# Revit family: AFX-Metropolitan-Semi_Flush
name_source: partatom
category: Lighting Fixtures
units: mm (PartAtom-declared; Revit-internal decimal feet)

## family parameters
Cut with Voids When Loaded = No
Host = Face
Light Source = No
Maintain Annotation Orientation = No
Part Type = Normal
Room Calculation Point = No
Round Connector Dimension = Use Diameter
Shared = No

## types (1)
- METC15
    Apparent Load = 0 VA
    Assembly Code = D5020200
    Canopy Finish = AFX - Paint Black
    Default Elevation = 48"
    Depth = 7 3/4"
    Description = LED Semi Flush - 15 1/2" Dia x 7 3/4"D
    Diameter = 15 1/2"
    Diffuser Finish = AFX - Diffuser
    Keynote = 12500
    Manufacturer = AFX Inc
    Model = METC15
    Power Factor = 1
    Product Documentation Link = https://www.afxinc.com
    Revit Model Built By = https://www.servex-us.com
    Support Finish = AFX - Paint Black
    Sustainability = https://lamprecycle.org
    Type Comments = Metropolitan
    URL = https://www.afxinc.com
    Voltage = 120 V
    Wattage Comments = 18W

## geometry (parser evidence)
native form markers: Sweep x3
no freeform markers — native parametric forms only
